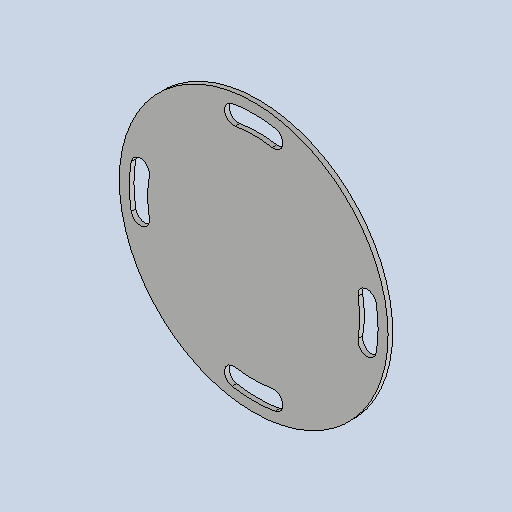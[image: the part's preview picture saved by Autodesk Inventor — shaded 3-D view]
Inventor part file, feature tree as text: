
AUTODESK INVENTOR PART (.ipt)
format: ipt  version: 2025 (Build 290162010, 162A)  size: 169,472 bytes
history: native  units: mm
features: sketch x2, sheet_metal_op x1, extrude x1, pattern_circular x1, other x1
ambient origin geometry x8: Origin, YZ Plane, XZ Plane, XY Plane, X Axis, Y Axis, Z Axis, Center Point
bodies: Solid1 (feature_tree)
feature tree (6):
  sheet_metal_op  "Face1"
  extrude  "Extrusion1"  Depth=3.0mm
  pattern_circular  "Circular Pattern1"  Count=4 Angle=360.0deg
  sketch  "Sketch1"  dims[d0=175.0mm d1=3.0mm]
  other  "Plate1"
  sketch  "Sketch2"  dims[d11=0.0mm d12=0.0mm d13=40.0mm d14=360.0deg d19=12.0mm d20=3.490659mm d21=75.0mm]
